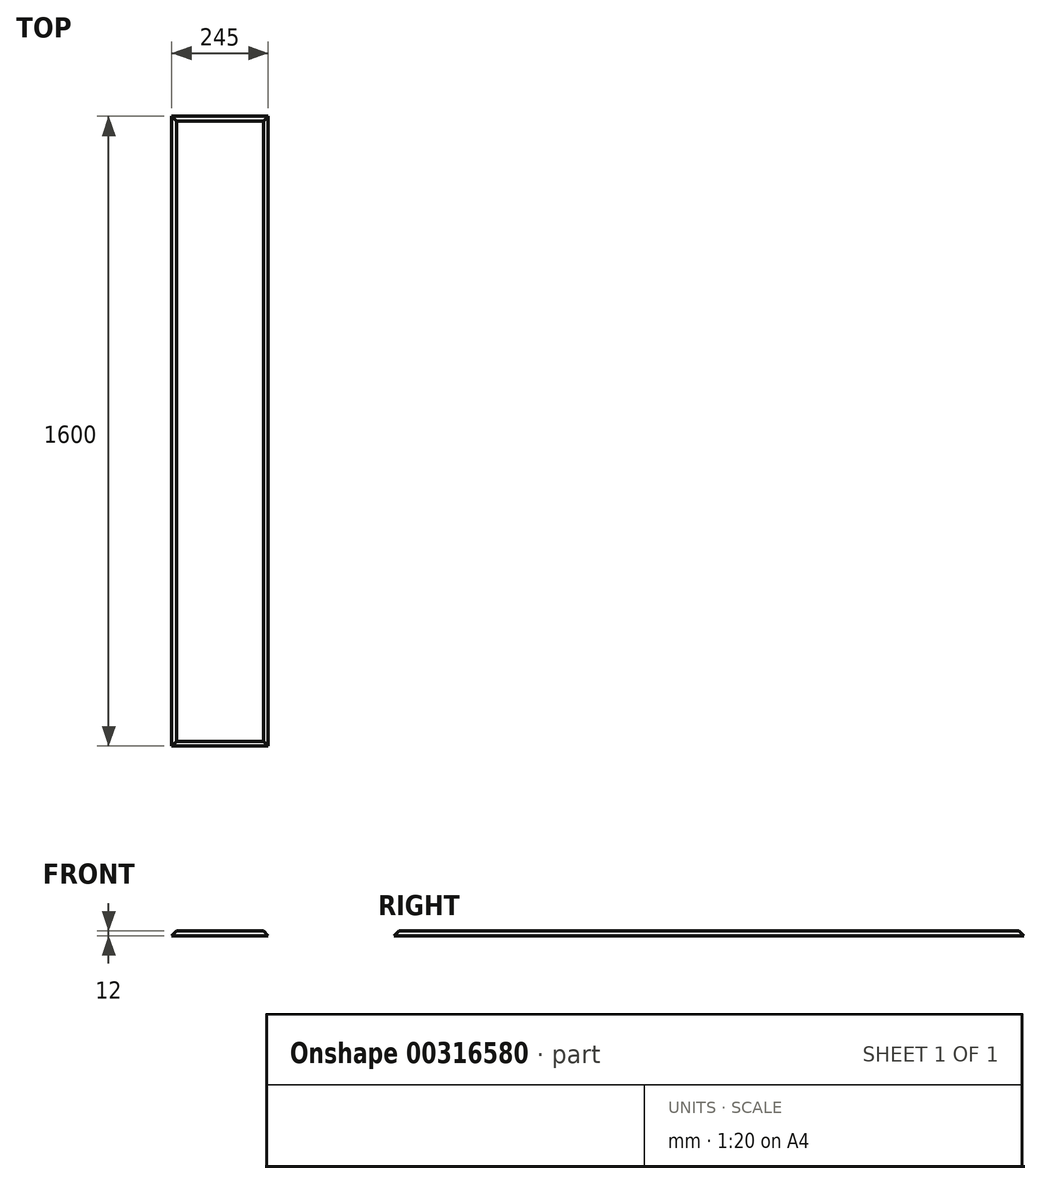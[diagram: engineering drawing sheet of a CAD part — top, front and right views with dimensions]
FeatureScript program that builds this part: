
annotation { "Feature Type Name" : "Feature", "Feature Type Description" : "" }
export const myFeature = defineFeature(function(context is Context, id is Id, definition is map)
    precondition{}
    {
        {
            var Q0;
            Q0=qCreatedBy(makeId("Top.planeOp"),FACE);
            var sketch = newSketch(context, id + "F0", { "sketchPlane" : qUnion([Q0])});
            skLineSegment(sketch, "E0.bottom", {"start": v(122.5, 800) * mm, "end": v(-122.5, 800) * mm});
            skLineSegment(sketch, "E0.top", {"start": v(122.5, -800) * mm, "end": v(-122.5, -800) * mm});
            skLineSegment(sketch, "E0.left", {"start": v(122.5, 800) * mm, "end": v(122.5, -800) * mm});
            skLineSegment(sketch, "E0.right", {"start": v(-122.5, 800) * mm, "end": v(-122.5, -800) * mm});
            skPoint(sketch, "E0.middle", {"position": v(0, 0) * mm});
            skSolve(sketch);
        }
        {
            var Q0;
            Q0 = qSketchRegion(id + "F0", true);
            extrude(context, id + "F1", {"entities" : qUnion([Q0]), "oppositeDirection" : true, "depth" : 12 * mm});
        }
        {
            var Q0;
            Q0=makeQuery(id+"F1.opExtrude","CAP_EDGE",EDGE,{"disambiguationData":[OSD([sQuery(id+"F0.wireOp",EDGE,"E0.top")])],"isStart":true});
            var Q1;
            Q1=makeQuery(id+"F1.opExtrude","CAP_EDGE",EDGE,{"disambiguationData":[OSD([sQuery(id+"F0.wireOp",EDGE,"E0.left")])],"isStart":true});
            var Q2;
            Q2=makeQuery(id+"F1.opExtrude","CAP_EDGE",EDGE,{"disambiguationData":[OSD([sQuery(id+"F0.wireOp",EDGE,"E0.right")])],"isStart":true});
            var Q3;
            Q3=makeQuery(id+"F1.opExtrude","CAP_EDGE",EDGE,{"disambiguationData":[OSD([sQuery(id+"F0.wireOp",EDGE,"E0.bottom")])],"isStart":true});
            chamfer(context, id + "F2", {"entities" : qUnion([Q0, Q1, Q2, Q3]), "width" : 12 * mm, "tangentPropagation" : true});
        }
    });
